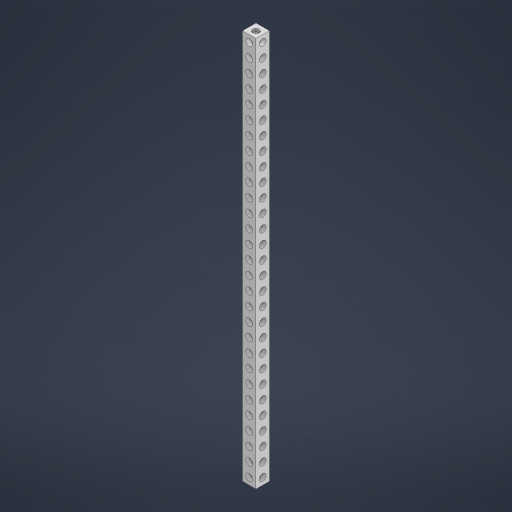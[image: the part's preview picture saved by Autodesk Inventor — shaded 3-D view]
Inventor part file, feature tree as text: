
AUTODESK INVENTOR PART (.ipt)
format: ipt  version: 2023 (Build 270158000, 158)  size: 1,287,680 bytes
history: native  units: in
note: dims shown in document units (in); Inventor stores cm internally (conversion verified against a paired STEP export)
features: mirror x1
ambient origin geometry x8: Origin, YZ Plane, XZ Plane, XY Plane, X Axis, Y Axis, Z Axis, Center Point
bodies: Solid1 (feature_tree)
feature tree (1):
  mirror  "Mirror3"
